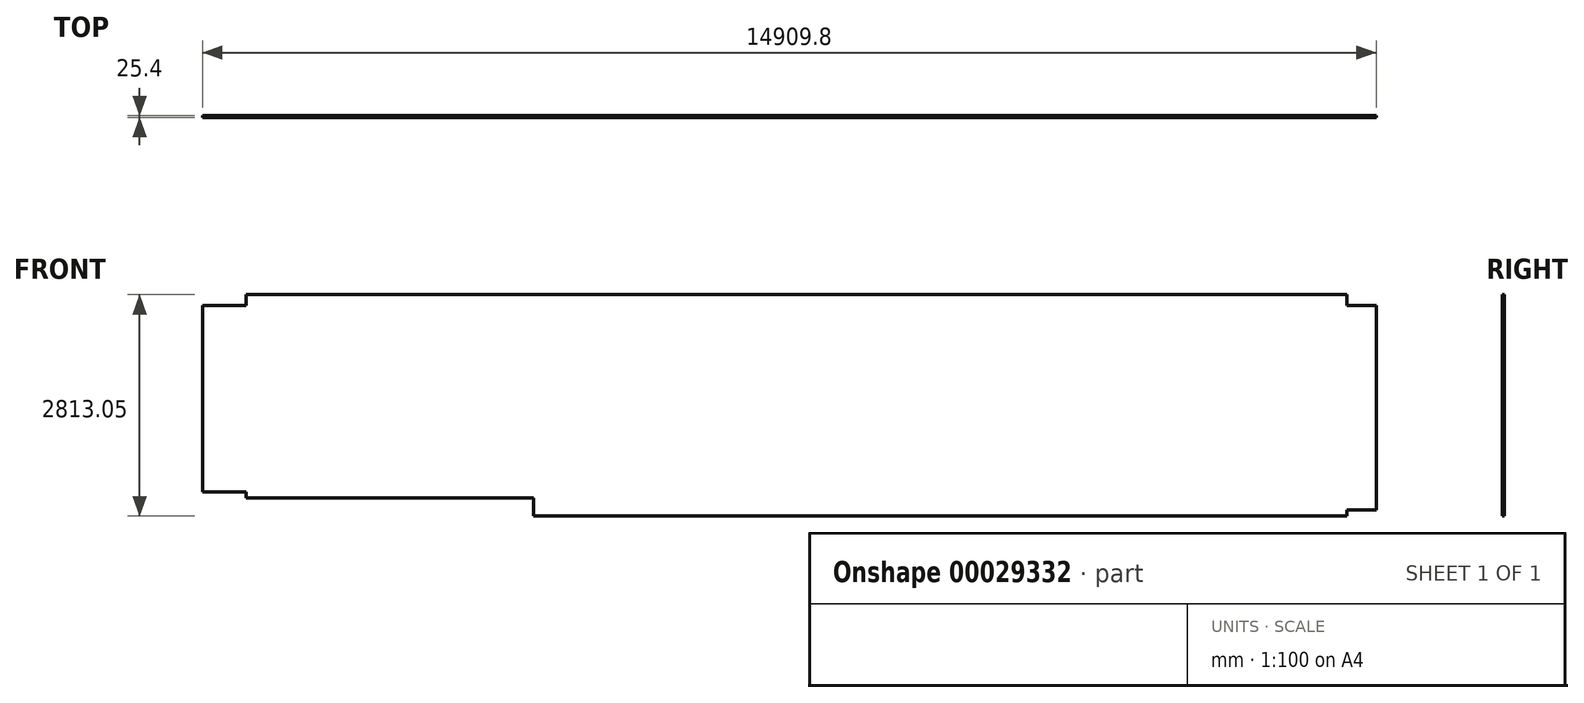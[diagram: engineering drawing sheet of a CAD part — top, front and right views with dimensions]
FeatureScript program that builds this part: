
annotation { "Feature Type Name" : "Feature", "Feature Type Description" : "" }
export const myFeature = defineFeature(function(context is Context, id is Id, definition is map)
    precondition{}
    {
        {
            var Q0;
            Q0=qCreatedBy(makeId("Front.planeOp"),FACE);
            var sketch = newSketch(context, id + "F0", { "sketchPlane" : qUnion([Q0])});
            skLineSegment(sketch, "E0.bottom", {"start": v(4203.7, 0) * mm, "end": v(14535.15, 0) * mm});
            skLineSegment(sketch, "E0.top", {"start": v(552.45, 2813.05) * mm, "end": v(14535.15, 2813.05) * mm});
            skLineSegment(sketch, "E0.left", {"start": v(0, 304.8) * mm, "end": v(0, 2673.35) * mm});
            skLineSegment(sketch, "E0.right", {"start": v(14909.8, 76.2) * mm, "end": v(14909.8, 2673.35) * mm});
            skLineSegment(sketch, "E1", {"start": v(0, 2673.35) * mm, "end": v(552.45, 2673.35) * mm});
            skLineSegment(sketch, "E2", {"start": v(552.45, 2673.35) * mm, "end": v(552.45, 2813.05) * mm});
            skLineSegment(sketch, "E3", {"start": v(14535.15, 2813.05) * mm, "end": v(14535.15, 2673.35) * mm});
            skLineSegment(sketch, "E4", {"start": v(14535.15, 2673.35) * mm, "end": v(14909.8, 2673.35) * mm});
            skLineSegment(sketch, "E5", {"start": v(14535.15, 0) * mm, "end": v(14535.15, 76.2) * mm});
            skLineSegment(sketch, "E6", {"start": v(14535.15, 76.2) * mm, "end": v(14909.8, 76.2) * mm});
            skLineSegment(sketch, "E7", {"start": v(4203.7, 0) * mm, "end": v(4203.7, 228.6) * mm});
            skLineSegment(sketch, "E8", {"start": v(4203.7, 228.6) * mm, "end": v(552.45, 228.6) * mm});
            skLineSegment(sketch, "E9", {"start": v(552.45, 228.6) * mm, "end": v(552.45, 304.8) * mm});
            skLineSegment(sketch, "E10", {"start": v(552.45, 304.8) * mm, "end": v(0, 304.8) * mm});
            skPoint(sketch, "E11.orphan", {"position": v(552.45, 0) * mm});
            skSolve(sketch);
        }
        {
            var Q0;
            Q0 = qSketchRegion(id + "F0", true);
            extrude(context, id + "F1", {"entities" : qUnion([Q0]), "depth" : 25.4 * mm});
        }
    });
